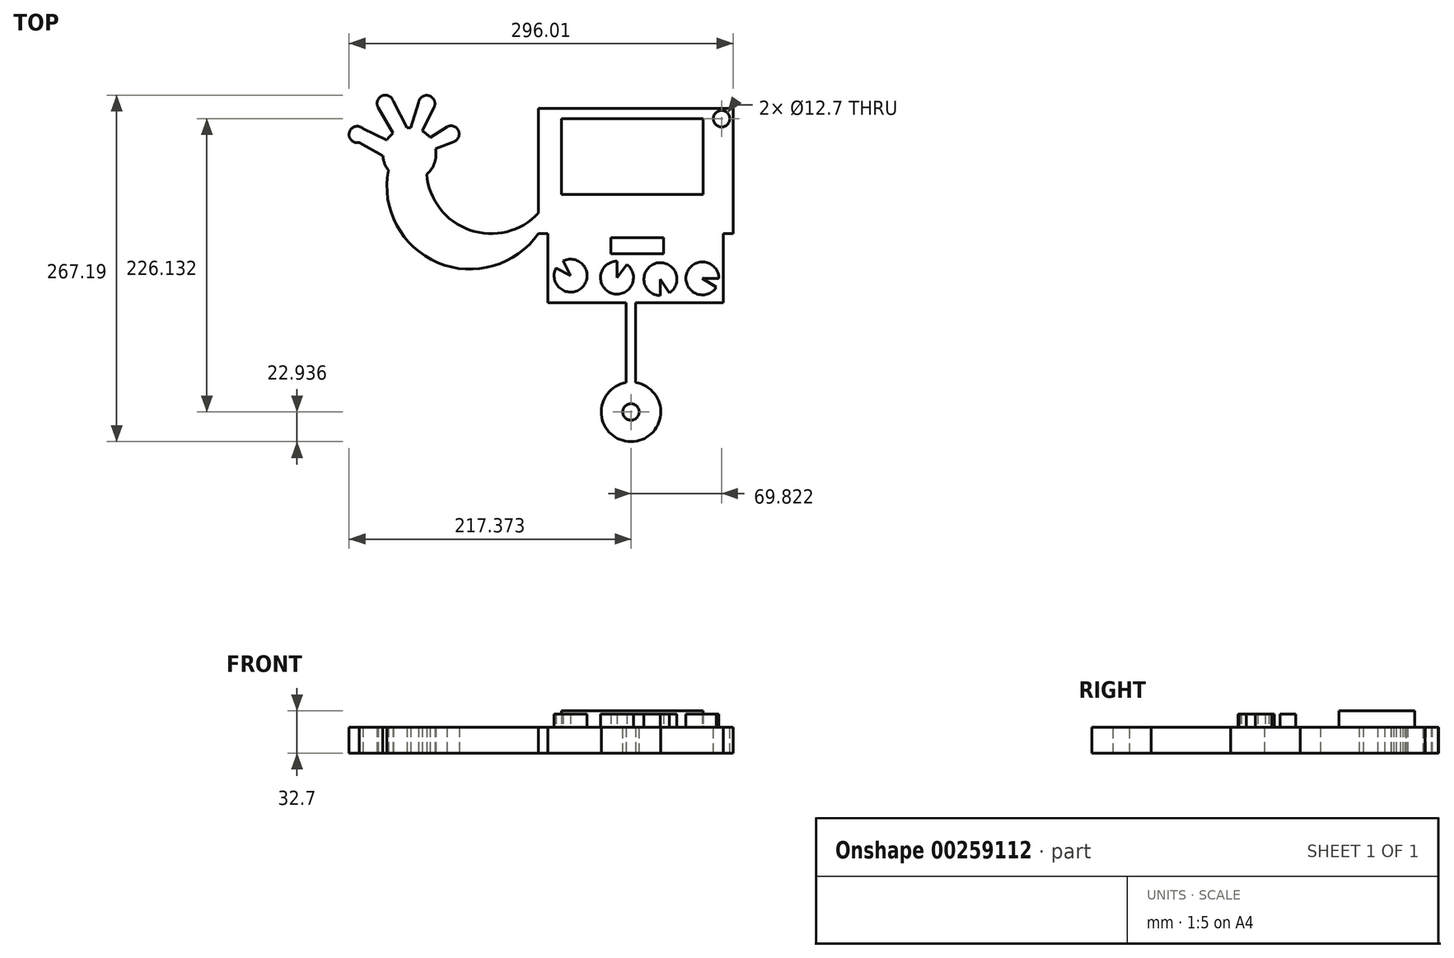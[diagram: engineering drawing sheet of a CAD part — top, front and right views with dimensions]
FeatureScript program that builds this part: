
annotation { "Feature Type Name" : "Feature", "Feature Type Description" : "" }
export const myFeature = defineFeature(function(context is Context, id is Id, definition is map)
    precondition{}
    {
        {
            var Q0;
            Q0=qCreatedBy(makeId("Top.planeOp"),FACE);
            var sketch = newSketch(context, id + "F0", { "sketchPlane" : qUnion([Q0])});
            skLineSegment(sketch, "E0.bottom", {"start": v(-67.58, -75) * mm, "end": v(67.58, -75) * mm});
            skLineSegment(sketch, "E0.top", {"start": v(-75, 75) * mm, "end": v(75, 75) * mm});
            skLineSegment(sketch, "E0.left", {"start": v(-75, -21.37) * mm, "end": v(-75, 75) * mm});
            skLineSegment(sketch, "E0.right", {"start": v(75, -21.37) * mm, "end": v(75, 75) * mm});
            skPoint(sketch, "E0.middle", {"position": v(0, 0) * mm});
            skLineSegment(sketch, "E1", {"start": v(-75, -21.37) * mm, "end": v(-67.58, -21.37) * mm});
            skLineSegment(sketch, "E2", {"start": v(-67.58, -21.37) * mm, "end": v(-67.58, -75) * mm});
            skLineSegment(sketch, "E3", {"start": v(67.58, -21.37) * mm, "end": v(75, -21.37) * mm});
            skLineSegment(sketch, "E4", {"start": v(67.58, -21.37) * mm, "end": v(67.58, -75) * mm});
            skLineSegment(sketch, "E5", {"start": v(-7.27, -75) * mm, "end": v(-7.27, -136.41) * mm});
            skCircle(sketch, "E6", {"center": v(-3.64, -159.05) * mm, "radius": 22.93 * mm});
            skCircle(sketch, "E7", {"center": v(-3.64, -159.05) * mm, "radius": 4.25 * mm});
            skLineSegment(sketch, "E8.trimOffspring", {"start": v(0, -136.41) * mm, "end": v(0, -75) * mm});
            skArc(sketch, "E9", {"start": v(-190.7, 27.24) * mm, "mid": v(-152.56, -43.97) * mm, "end": v(-75, -21.37) * mm});
            skLineSegment(sketch, "E10", {"start": v(0, -42.13) * mm, "end": v(0, -75) * mm, "construction": true});
            skArc(sketch, "E11.MirrorCS", {"start": v(190.7, 27.24) * mm, "mid": v(152.56, -43.97) * mm, "end": v(75, -21.37) * mm});
            skArc(sketch, "E12", {"start": v(-161.15, 24.18) * mm, "mid": v(-127.81, -18.85) * mm, "end": v(-75, -5.67) * mm});
            skArc(sketch, "E13.MirrorCS", {"start": v(161.15, 24.18) * mm, "mid": v(127.81, -18.85) * mm, "end": v(75, -5.67) * mm});
            skArc(sketch, "E14", {"start": v(-161.15, 24.18) * mm, "mid": v(-155.11, 33.1) * mm, "end": v(-154.43, 43.84) * mm});
            skArc(sketch, "E15.MirrorC", {"start": v(161.15, 24.18) * mm, "mid": v(155.11, 33.1) * mm, "end": v(154.43, 43.84) * mm});
            skArc(sketch, "E16", {"start": v(-210.14, 59.34) * mm, "mid": v(-220.78, 56.58) * mm, "end": v(-213.12, 48.7) * mm});
            skArc(sketch, "E17", {"start": v(-186.9, 80.39) * mm, "mid": v(-195.48, 84.73) * mm, "end": v(-198.53, 75.61) * mm});
            skArc(sketch, "E18", {"start": v(-155.48, 75.8) * mm, "mid": v(-159.23, 84.75) * mm, "end": v(-167.43, 79.57) * mm});
            skArc(sketch, "E19", {"start": v(-140.2, 49.3) * mm, "mid": v(-136.86, 58.2) * mm, "end": v(-146.08, 60.46) * mm});
            skLineSegment(sketch, "E20", {"start": v(-210.14, 59.34) * mm, "end": v(-191.76, 50.67) * mm});
            skLineSegment(sketch, "E21", {"start": v(-213.12, 48.7) * mm, "end": v(-194.9, 38.48) * mm});
            skArc(sketch, "E22.trimOffspring", {"start": v(-194.9, 38.48) * mm, "mid": v(-193.65, 32.54) * mm, "end": v(-190.7, 27.24) * mm});
            skLineSegment(sketch, "E23", {"start": v(-198.53, 75.61) * mm, "end": v(-187.14, 55.8) * mm});
            skLineSegment(sketch, "E24", {"start": v(-186.9, 80.39) * mm, "end": v(-176.4, 60.09) * mm});
            skArc(sketch, "E25.trimOffspring", {"start": v(-187.14, 55.8) * mm, "mid": v(-189.67, 53.43) * mm, "end": v(-191.76, 50.67) * mm});
            skLineSegment(sketch, "E26", {"start": v(-155.48, 75.8) * mm, "end": v(-164.74, 57.71) * mm});
            skLineSegment(sketch, "E27", {"start": v(-167.43, 79.57) * mm, "end": v(-173.43, 60.15) * mm});
            skArc(sketch, "E28.trimOffspring", {"start": v(-173.43, 60.15) * mm, "mid": v(-174.91, 60.18) * mm, "end": v(-176.4, 60.09) * mm});
            skLineSegment(sketch, "E29", {"start": v(-140.2, 49.3) * mm, "end": v(-154.43, 43.84) * mm});
            skLineSegment(sketch, "E30", {"start": v(-145.68, 60.72) * mm, "end": v(-158.55, 52.56) * mm});
            skArc(sketch, "E31.trimOffspring", {"start": v(-158.55, 52.56) * mm, "mid": v(-161.39, 55.45) * mm, "end": v(-164.74, 57.71) * mm});
            skArc(sketch, "E32.MirrorCS", {"start": v(187.14, 55.8) * mm, "mid": v(189.67, 53.43) * mm, "end": v(191.76, 50.67) * mm});
            skArc(sketch, "E33.MirrorCS", {"start": v(173.43, 60.15) * mm, "mid": v(174.91, 60.18) * mm, "end": v(176.4, 60.09) * mm});
            skArc(sketch, "E34.MirrorCS", {"start": v(158.55, 52.56) * mm, "mid": v(161.39, 55.45) * mm, "end": v(164.74, 57.71) * mm});
            skLineSegment(sketch, "E35.MirrorCS", {"start": v(198.53, 75.61) * mm, "end": v(187.14, 55.8) * mm});
            skArc(sketch, "E36.MirrorCS", {"start": v(210.14, 59.34) * mm, "mid": v(220.78, 56.58) * mm, "end": v(213.12, 48.7) * mm});
            skArc(sketch, "E37.MirrorCS", {"start": v(194.9, 38.48) * mm, "mid": v(193.65, 32.54) * mm, "end": v(190.7, 27.24) * mm});
            skArc(sketch, "E38.MirrorCS", {"start": v(140.2, 49.3) * mm, "mid": v(136.86, 58.2) * mm, "end": v(146.08, 60.46) * mm});
            skLineSegment(sketch, "E39.MirrorCS", {"start": v(140.2, 49.3) * mm, "end": v(154.43, 43.84) * mm});
            skLineSegment(sketch, "E40.MirrorCS", {"start": v(213.12, 48.7) * mm, "end": v(194.9, 38.48) * mm});
            skArc(sketch, "E41.MirrorCS", {"start": v(155.48, 75.8) * mm, "mid": v(159.23, 84.75) * mm, "end": v(167.43, 79.57) * mm});
            skLineSegment(sketch, "E42.MirrorCS", {"start": v(155.48, 75.8) * mm, "end": v(164.74, 57.71) * mm});
            skLineSegment(sketch, "E43.MirrorCS", {"start": v(145.68, 60.72) * mm, "end": v(158.55, 52.56) * mm});
            skArc(sketch, "E44.MirrorCS", {"start": v(186.9, 80.39) * mm, "mid": v(195.48, 84.73) * mm, "end": v(198.53, 75.61) * mm});
            skLineSegment(sketch, "E45.MirrorCS", {"start": v(186.9, 80.39) * mm, "end": v(176.4, 60.09) * mm});
            skLineSegment(sketch, "E46.MirrorCS", {"start": v(167.43, 79.57) * mm, "end": v(173.43, 60.15) * mm});
            skLineSegment(sketch, "E47.MirrorCS", {"start": v(210.14, 59.34) * mm, "end": v(191.76, 50.67) * mm});
            skPoint(sketch, "E48.orphan", {"position": v(-75, -75) * mm});
            skPoint(sketch, "E49.orphan", {"position": v(75, -75) * mm});
            skSolve(sketch);
        }
        {
            var Q0;
            {var subQ1=sQuery(id+"F0.wireOp",EDGE,"E0.top");Q0=makeQuery(id+"F0.imprint","IMPRINT",FACE,{"disambiguationData":[TD([[makeQuery(id+"F0.imprint","IMPRINT",EDGE,{"derivedFrom":subQ1}),-1.0]])]});}
            var Q1;
            {var subQ4=sQuery(id+"F0.wireOp",EDGE,"E9");Q1=makeQuery(id+"F0.imprint","IMPRINT",FACE,{"disambiguationData":[TD([[makeQuery(id+"F0.imprint","IMPRINT",EDGE,{"derivedFrom":subQ4}),1.0]])]});}
            var Q2;
            {var subQ6=sQuery(id+"F0.wireOp",EDGE,"E11.MirrorCS");Q2=makeQuery(id+"F0.imprint","IMPRINT",FACE,{"disambiguationData":[TD([[makeQuery(id+"F0.imprint","IMPRINT",EDGE,{"derivedFrom":subQ6}),-1.0]])]});}
            var Q3;
            {var subQ0=sQuery(id+"F0.wireOp",EDGE,"E5");Q3=makeQuery(id+"F0.imprint","IMPRINT",FACE,{"disambiguationData":[TD([[makeQuery(id+"F0.imprint","IMPRINT",EDGE,{"derivedFrom":subQ0}),1.0]])]});}
            var Q4;
            Q4=makeQuery(id+"F0.imprint","IMPRINT",FACE,{"disambiguationData":[TD([[makeQuery(id+"F0.imprint","IMPRINT",EDGE,{"derivedFrom":sQuery(id+"F0.wireOp",EDGE,"E7")}),-1.0]])]});
            var Q5;
            Q5=makeQuery(id+"F0.imprint","IMPRINT",FACE,{"disambiguationData":[TD([[makeQuery(id+"F0.imprint","IMPRINT",EDGE,{"derivedFrom":sQuery(id+"F0.wireOp",EDGE,"E7")}),1.0]])]});
            extrude(context, id + "F1", {"entities" : qUnion([Q0, Q1, Q2, Q3, Q4, Q5]), "depth" : 20 * mm});
        }
        {
            var Q0;
            Q0=makeQuery(id+"F1.opExtrude","CAP_FACE",FACE,{"disambiguationData":[OSD([sQuery(id+"F0.wireOp",EDGE,"E0.bottom"),sQuery(id+"F0.wireOp",EDGE,"E0.top"),sQuery(id+"F0.wireOp",EDGE,"E0.left"),sQuery(id+"F0.wireOp",EDGE,"E0.right"),sQuery(id+"F0.wireOp",EDGE,"E1"),sQuery(id+"F0.wireOp",EDGE,"E2"),sQuery(id+"F0.wireOp",EDGE,"E3"),sQuery(id+"F0.wireOp",EDGE,"E4"),sQuery(id+"F0.wireOp",EDGE,"E5"),sQuery(id+"F0.wireOp",EDGE,"E6"),sQuery(id+"F0.wireOp",EDGE,"E8.trimOffspring"),sQuery(id+"F0.wireOp",EDGE,"E9"),sQuery(id+"F0.wireOp",EDGE,"E11.MirrorCS"),sQuery(id+"F0.wireOp",EDGE,"E12"),sQuery(id+"F0.wireOp",EDGE,"E13.MirrorCS"),sQuery(id+"F0.wireOp",EDGE,"E14"),sQuery(id+"F0.wireOp",EDGE,"E16"),sQuery(id+"F0.wireOp",EDGE,"E17"),sQuery(id+"F0.wireOp",EDGE,"E18"),sQuery(id+"F0.wireOp",EDGE,"E19"),sQuery(id+"F0.wireOp",EDGE,"E20"),sQuery(id+"F0.wireOp",EDGE,"E21"),sQuery(id+"F0.wireOp",EDGE,"E22.trimOffspring"),sQuery(id+"F0.wireOp",EDGE,"E23"),sQuery(id+"F0.wireOp",EDGE,"E24"),sQuery(id+"F0.wireOp",EDGE,"E25.trimOffspring"),sQuery(id+"F0.wireOp",EDGE,"E26"),sQuery(id+"F0.wireOp",EDGE,"E27"),sQuery(id+"F0.wireOp",EDGE,"E28.trimOffspring"),sQuery(id+"F0.wireOp",EDGE,"E29"),sQuery(id+"F0.wireOp",EDGE,"E30"),sQuery(id+"F0.wireOp",EDGE,"E31.trimOffspring"),sQuery(id+"F0.wireOp",EDGE,"E35.MirrorCS"),sQuery(id+"F0.wireOp",EDGE,"E36.MirrorCS"),sQuery(id+"F0.wireOp",EDGE,"E15.MirrorC"),sQuery(id+"F0.wireOp",EDGE,"E38.MirrorCS"),sQuery(id+"F0.wireOp",EDGE,"E39.MirrorCS"),sQuery(id+"F0.wireOp",EDGE,"E40.MirrorCS"),sQuery(id+"F0.wireOp",EDGE,"E41.MirrorCS"),sQuery(id+"F0.wireOp",EDGE,"E42.MirrorCS"),sQuery(id+"F0.wireOp",EDGE,"E43.MirrorCS"),sQuery(id+"F0.wireOp",EDGE,"E44.MirrorCS"),sQuery(id+"F0.wireOp",EDGE,"E45.MirrorCS"),sQuery(id+"F0.wireOp",EDGE,"E46.MirrorCS"),sQuery(id+"F0.wireOp",EDGE,"E47.MirrorCS"),sQuery(id+"F0.wireOp",EDGE,"E34.MirrorCS"),sQuery(id+"F0.wireOp",EDGE,"E33.MirrorCS"),sQuery(id+"F0.wireOp",EDGE,"E32.MirrorCS"),sQuery(id+"F0.wireOp",EDGE,"E37.MirrorCS")])],"isStart":false});
            var sketch = newSketch(context, id + "F2", { "sketchPlane" : qUnion([Q0])});
            skLineSegment(sketch, "E50.bottom", {"start": v(-19.06, -24.75) * mm, "end": v(21.38, -24.75) * mm});
            skLineSegment(sketch, "E50.top", {"start": v(-19.06, -37.01) * mm, "end": v(21.38, -37.01) * mm});
            skLineSegment(sketch, "E50.left", {"start": v(-19.06, -24.75) * mm, "end": v(-19.06, -37.01) * mm});
            skLineSegment(sketch, "E50.right", {"start": v(21.38, -24.75) * mm, "end": v(21.38, -37.01) * mm});
            skLineSegment(sketch, "E51", {"start": v(-8.67, -24.75) * mm, "end": v(-8.67, -37.01) * mm});
            skLineSegment(sketch, "E52", {"start": v(1.16, -24.75) * mm, "end": v(1.16, -37.01) * mm});
            skLineSegment(sketch, "E53", {"start": v(10.4, -24.75) * mm, "end": v(10.4, -37.01) * mm});
            skArc(sketch, "E54", {"start": v(-61.54, -48.19) * mm, "mid": v(-41.29, -62.98) * mm, "end": v(-55.89, -42.58) * mm});
            skArc(sketch, "E55", {"start": v(-14.44, -42.8) * mm, "mid": v(-18.53, -67.53) * mm, "end": v(-6.7, -45.43) * mm});
            skArc(sketch, "E56", {"start": v(26.07, -67.25) * mm, "mid": v(15.4, -44.5) * mm, "end": v(19.07, -69.36) * mm});
            skArc(sketch, "E57", {"start": v(64.12, -56.08) * mm, "mid": v(39.22, -52.55) * mm, "end": v(62.16, -62.86) * mm});
            skPoint(sketch, "E58.startSnap0", {"position": v(-67.58, -48.19) * mm});
            skLineSegment(sketch, "E59", {"start": v(-55.89, -42.58) * mm, "end": v(-50.23, -53.95) * mm});
            skPoint(sketch, "E59.startSnap0", {"position": v(-55.89, -51.07) * mm});
            skLineSegment(sketch, "E60", {"start": v(-14.44, -55.5) * mm, "end": v(-14.44, -42.8) * mm});
            skLineSegment(sketch, "E61", {"start": v(-14.44, -55.5) * mm, "end": v(-6.7, -45.43) * mm});
            skLineSegment(sketch, "E62", {"start": v(19.07, -56.66) * mm, "end": v(19.07, -69.36) * mm});
            skLineSegment(sketch, "E63", {"start": v(19.07, -56.66) * mm, "end": v(26.07, -67.25) * mm});
            skLineSegment(sketch, "E64", {"start": v(51.42, -56.08) * mm, "end": v(64.12, -56.08) * mm});
            skLineSegment(sketch, "E65", {"start": v(64.12, -56.08) * mm, "end": v(51.42, -56.08) * mm});
            skLineSegment(sketch, "E66", {"start": v(51.42, -56.08) * mm, "end": v(62.16, -62.86) * mm});
            skPoint(sketch, "E67.orphan", {"position": v(-61.54, -48.19) * mm});
            skLineSegment(sketch, "E68", {"start": v(-61.54, -48.19) * mm, "end": v(-50.23, -53.95) * mm});
            skSolve(sketch);
        }
        {
            var Q0;
            Q0 = qSketchRegion(id + "F2", true);
            extrude(context, id + "F3", {"entities" : qUnion([Q0]), "operationType" : NewBodyOperationType.ADD, "depth" : 10.16 * mm});
        }
        {
            var Q0;
            Q0=makeQuery(id+"F1.opExtrude","CAP_FACE",FACE,{"disambiguationData":[OSD([sQuery(id+"F0.wireOp",EDGE,"E0.bottom"),sQuery(id+"F0.wireOp",EDGE,"E0.top"),sQuery(id+"F0.wireOp",EDGE,"E0.left"),sQuery(id+"F0.wireOp",EDGE,"E0.right"),sQuery(id+"F0.wireOp",EDGE,"E1"),sQuery(id+"F0.wireOp",EDGE,"E2"),sQuery(id+"F0.wireOp",EDGE,"E3"),sQuery(id+"F0.wireOp",EDGE,"E4"),sQuery(id+"F0.wireOp",EDGE,"E5"),sQuery(id+"F0.wireOp",EDGE,"E6"),sQuery(id+"F0.wireOp",EDGE,"E8.trimOffspring"),sQuery(id+"F0.wireOp",EDGE,"E9"),sQuery(id+"F0.wireOp",EDGE,"E11.MirrorCS"),sQuery(id+"F0.wireOp",EDGE,"E12"),sQuery(id+"F0.wireOp",EDGE,"E13.MirrorCS"),sQuery(id+"F0.wireOp",EDGE,"E14"),sQuery(id+"F0.wireOp",EDGE,"E16"),sQuery(id+"F0.wireOp",EDGE,"E17"),sQuery(id+"F0.wireOp",EDGE,"E18"),sQuery(id+"F0.wireOp",EDGE,"E19"),sQuery(id+"F0.wireOp",EDGE,"E20"),sQuery(id+"F0.wireOp",EDGE,"E21"),sQuery(id+"F0.wireOp",EDGE,"E22.trimOffspring"),sQuery(id+"F0.wireOp",EDGE,"E23"),sQuery(id+"F0.wireOp",EDGE,"E24"),sQuery(id+"F0.wireOp",EDGE,"E25.trimOffspring"),sQuery(id+"F0.wireOp",EDGE,"E26"),sQuery(id+"F0.wireOp",EDGE,"E27"),sQuery(id+"F0.wireOp",EDGE,"E28.trimOffspring"),sQuery(id+"F0.wireOp",EDGE,"E29"),sQuery(id+"F0.wireOp",EDGE,"E30"),sQuery(id+"F0.wireOp",EDGE,"E31.trimOffspring"),sQuery(id+"F0.wireOp",EDGE,"E35.MirrorCS"),sQuery(id+"F0.wireOp",EDGE,"E36.MirrorCS"),sQuery(id+"F0.wireOp",EDGE,"E15.MirrorC"),sQuery(id+"F0.wireOp",EDGE,"E38.MirrorCS"),sQuery(id+"F0.wireOp",EDGE,"E39.MirrorCS"),sQuery(id+"F0.wireOp",EDGE,"E40.MirrorCS"),sQuery(id+"F0.wireOp",EDGE,"E41.MirrorCS"),sQuery(id+"F0.wireOp",EDGE,"E42.MirrorCS"),sQuery(id+"F0.wireOp",EDGE,"E43.MirrorCS"),sQuery(id+"F0.wireOp",EDGE,"E44.MirrorCS"),sQuery(id+"F0.wireOp",EDGE,"E45.MirrorCS"),sQuery(id+"F0.wireOp",EDGE,"E46.MirrorCS"),sQuery(id+"F0.wireOp",EDGE,"E47.MirrorCS"),sQuery(id+"F0.wireOp",EDGE,"E34.MirrorCS"),sQuery(id+"F0.wireOp",EDGE,"E33.MirrorCS"),sQuery(id+"F0.wireOp",EDGE,"E32.MirrorCS"),sQuery(id+"F0.wireOp",EDGE,"E37.MirrorCS")])],"isStart":false});
            var sketch = newSketch(context, id + "F4", { "sketchPlane" : qUnion([Q0])});
            skLineSegment(sketch, "E69.bottom", {"start": v(-57.22, 67.08) * mm, "end": v(52, 67.08) * mm});
            skLineSegment(sketch, "E69.top", {"start": v(-57.22, 8.66) * mm, "end": v(52, 8.66) * mm});
            skLineSegment(sketch, "E69.left", {"start": v(-57.22, 67.08) * mm, "end": v(-57.22, 8.66) * mm});
            skLineSegment(sketch, "E69.right", {"start": v(52, 67.08) * mm, "end": v(52, 8.66) * mm});
            skSolve(sketch);
        }
        {
            var Q0;
            Q0=makeQuery(id+"F1.opExtrude","CAP_FACE",FACE,{"disambiguationData":[OSD([sQuery(id+"F0.wireOp",EDGE,"E0.bottom"),sQuery(id+"F0.wireOp",EDGE,"E0.top"),sQuery(id+"F0.wireOp",EDGE,"E0.left"),sQuery(id+"F0.wireOp",EDGE,"E0.right"),sQuery(id+"F0.wireOp",EDGE,"E1"),sQuery(id+"F0.wireOp",EDGE,"E2"),sQuery(id+"F0.wireOp",EDGE,"E3"),sQuery(id+"F0.wireOp",EDGE,"E4"),sQuery(id+"F0.wireOp",EDGE,"E5"),sQuery(id+"F0.wireOp",EDGE,"E6"),sQuery(id+"F0.wireOp",EDGE,"E8.trimOffspring"),sQuery(id+"F0.wireOp",EDGE,"E9"),sQuery(id+"F0.wireOp",EDGE,"E11.MirrorCS"),sQuery(id+"F0.wireOp",EDGE,"E12"),sQuery(id+"F0.wireOp",EDGE,"E13.MirrorCS"),sQuery(id+"F0.wireOp",EDGE,"E14"),sQuery(id+"F0.wireOp",EDGE,"E16"),sQuery(id+"F0.wireOp",EDGE,"E17"),sQuery(id+"F0.wireOp",EDGE,"E18"),sQuery(id+"F0.wireOp",EDGE,"E19"),sQuery(id+"F0.wireOp",EDGE,"E20"),sQuery(id+"F0.wireOp",EDGE,"E21"),sQuery(id+"F0.wireOp",EDGE,"E22.trimOffspring"),sQuery(id+"F0.wireOp",EDGE,"E23"),sQuery(id+"F0.wireOp",EDGE,"E24"),sQuery(id+"F0.wireOp",EDGE,"E25.trimOffspring"),sQuery(id+"F0.wireOp",EDGE,"E26"),sQuery(id+"F0.wireOp",EDGE,"E27"),sQuery(id+"F0.wireOp",EDGE,"E28.trimOffspring"),sQuery(id+"F0.wireOp",EDGE,"E29"),sQuery(id+"F0.wireOp",EDGE,"E30"),sQuery(id+"F0.wireOp",EDGE,"E31.trimOffspring"),sQuery(id+"F0.wireOp",EDGE,"E35.MirrorCS"),sQuery(id+"F0.wireOp",EDGE,"E36.MirrorCS"),sQuery(id+"F0.wireOp",EDGE,"E15.MirrorC"),sQuery(id+"F0.wireOp",EDGE,"E38.MirrorCS"),sQuery(id+"F0.wireOp",EDGE,"E39.MirrorCS"),sQuery(id+"F0.wireOp",EDGE,"E40.MirrorCS"),sQuery(id+"F0.wireOp",EDGE,"E41.MirrorCS"),sQuery(id+"F0.wireOp",EDGE,"E42.MirrorCS"),sQuery(id+"F0.wireOp",EDGE,"E43.MirrorCS"),sQuery(id+"F0.wireOp",EDGE,"E44.MirrorCS"),sQuery(id+"F0.wireOp",EDGE,"E45.MirrorCS"),sQuery(id+"F0.wireOp",EDGE,"E46.MirrorCS"),sQuery(id+"F0.wireOp",EDGE,"E47.MirrorCS"),sQuery(id+"F0.wireOp",EDGE,"E34.MirrorCS"),sQuery(id+"F0.wireOp",EDGE,"E33.MirrorCS"),sQuery(id+"F0.wireOp",EDGE,"E32.MirrorCS"),sQuery(id+"F0.wireOp",EDGE,"E37.MirrorCS")])],"isStart":false});
            var sketch = newSketch(context, id + "F5", { "sketchPlane" : qUnion([Q0])});
            skCircle(sketch, "E70", {"center": v(-3.64, -159.05) * mm, "radius": 6.35 * mm});
            skSolve(sketch);
        }
        {
            var Q0;
            Q0=makeQuery(id+"F5.imprint","IMPRINT",FACE,{"disambiguationData":[TD([[makeQuery(id+"F5.imprint","IMPRINT",EDGE,{"derivedFrom":sQuery(id+"F5.wireOp",EDGE,"E70")}),1.0]])]});
            extrude(context, id + "F6", {"entities" : qUnion([Q0]), "operationType" : NewBodyOperationType.REMOVE, "oppositeDirection" : true, "depth" : 25.4 * mm});
        }
        {
            var Q0;
            Q0=makeQuery(id+"F1.opExtrude","CAP_FACE",FACE,{"disambiguationData":[OSD([sQuery(id+"F0.wireOp",EDGE,"E0.bottom"),sQuery(id+"F0.wireOp",EDGE,"E0.top"),sQuery(id+"F0.wireOp",EDGE,"E0.left"),sQuery(id+"F0.wireOp",EDGE,"E0.right"),sQuery(id+"F0.wireOp",EDGE,"E1"),sQuery(id+"F0.wireOp",EDGE,"E2"),sQuery(id+"F0.wireOp",EDGE,"E3"),sQuery(id+"F0.wireOp",EDGE,"E4"),sQuery(id+"F0.wireOp",EDGE,"E5"),sQuery(id+"F0.wireOp",EDGE,"E6"),sQuery(id+"F0.wireOp",EDGE,"E8.trimOffspring"),sQuery(id+"F0.wireOp",EDGE,"E9"),sQuery(id+"F0.wireOp",EDGE,"E11.MirrorCS"),sQuery(id+"F0.wireOp",EDGE,"E12"),sQuery(id+"F0.wireOp",EDGE,"E13.MirrorCS"),sQuery(id+"F0.wireOp",EDGE,"E14"),sQuery(id+"F0.wireOp",EDGE,"E16"),sQuery(id+"F0.wireOp",EDGE,"E17"),sQuery(id+"F0.wireOp",EDGE,"E18"),sQuery(id+"F0.wireOp",EDGE,"E19"),sQuery(id+"F0.wireOp",EDGE,"E20"),sQuery(id+"F0.wireOp",EDGE,"E21"),sQuery(id+"F0.wireOp",EDGE,"E22.trimOffspring"),sQuery(id+"F0.wireOp",EDGE,"E23"),sQuery(id+"F0.wireOp",EDGE,"E24"),sQuery(id+"F0.wireOp",EDGE,"E25.trimOffspring"),sQuery(id+"F0.wireOp",EDGE,"E26"),sQuery(id+"F0.wireOp",EDGE,"E27"),sQuery(id+"F0.wireOp",EDGE,"E28.trimOffspring"),sQuery(id+"F0.wireOp",EDGE,"E29"),sQuery(id+"F0.wireOp",EDGE,"E30"),sQuery(id+"F0.wireOp",EDGE,"E31.trimOffspring"),sQuery(id+"F0.wireOp",EDGE,"E35.MirrorCS"),sQuery(id+"F0.wireOp",EDGE,"E36.MirrorCS"),sQuery(id+"F0.wireOp",EDGE,"E15.MirrorC"),sQuery(id+"F0.wireOp",EDGE,"E38.MirrorCS"),sQuery(id+"F0.wireOp",EDGE,"E39.MirrorCS"),sQuery(id+"F0.wireOp",EDGE,"E40.MirrorCS"),sQuery(id+"F0.wireOp",EDGE,"E41.MirrorCS"),sQuery(id+"F0.wireOp",EDGE,"E42.MirrorCS"),sQuery(id+"F0.wireOp",EDGE,"E43.MirrorCS"),sQuery(id+"F0.wireOp",EDGE,"E44.MirrorCS"),sQuery(id+"F0.wireOp",EDGE,"E45.MirrorCS"),sQuery(id+"F0.wireOp",EDGE,"E46.MirrorCS"),sQuery(id+"F0.wireOp",EDGE,"E47.MirrorCS"),sQuery(id+"F0.wireOp",EDGE,"E34.MirrorCS"),sQuery(id+"F0.wireOp",EDGE,"E33.MirrorCS"),sQuery(id+"F0.wireOp",EDGE,"E32.MirrorCS"),sQuery(id+"F0.wireOp",EDGE,"E37.MirrorCS")])],"isStart":false});
            var sketch = newSketch(context, id + "F7", { "sketchPlane" : qUnion([Q0])});
            skCircle(sketch, "E71", {"center": v(66.19, 67.08) * mm, "radius": 6.35 * mm});
            skSolve(sketch);
        }
        {
            var Q0;
            Q0=makeQuery(id+"F7.imprint","IMPRINT",FACE,{"disambiguationData":[TD([[makeQuery(id+"F7.imprint","IMPRINT",EDGE,{"derivedFrom":sQuery(id+"F7.wireOp",EDGE,"E71")}),1.0]])]});
            extrude(context, id + "F8", {"entities" : qUnion([Q0]), "operationType" : NewBodyOperationType.REMOVE, "oppositeDirection" : true, "depth" : 25.4 * mm});
        }
        {
            var Q0;
            {var subQ0=sQuery(id+"F4.wireOp",EDGE,"E69.left");var subQ1=sQuery(id+"F4.wireOp",EDGE,"E69.bottom");var subQ2=makeQuery(id+"F4.imprint","INTERSECT",VERTEX,{"derivedFrom":[subQ1,subQ0]});Q0=makeQuery(id+"F4.imprint","IMPRINT",FACE,{"disambiguationData":[TD([[makeQuery(id+"F4.imprint","IMPRINT",EDGE,{"disambiguationData":[TD([[subQ2,-1.0]])],"derivedFrom":subQ1}),-1.0]])]});}
            var Q1;
            {var subQ0=sQuery(id+"F4.wireOp",EDGE,"6969bc10-0764-4b5e-9f94-18c3d4fac763");var subQ1=sQuery(id+"F4.wireOp",EDGE,"E69.bottom");var subQ2=makeQuery(id+"F4.imprint","INTERSECT",VERTEX,{"derivedFrom":[subQ1,subQ0]});Q1=makeQuery(id+"F4.imprint","IMPRINT",FACE,{"disambiguationData":[TD([[makeQuery(id+"F4.imprint","IMPRINT",EDGE,{"disambiguationData":[TD([[subQ2,-1.0]])],"derivedFrom":subQ1}),-1.0]])]});}
            var Q2;
            {var subQ0=sQuery(id+"F4.wireOp",EDGE,"04714c49-f67c-4b11-ac7b-a62ad5dfcefc");var subQ1=sQuery(id+"F4.wireOp",EDGE,"E69.bottom");var subQ2=makeQuery(id+"F4.imprint","INTERSECT",VERTEX,{"derivedFrom":[subQ1,subQ0]});Q2=makeQuery(id+"F4.imprint","IMPRINT",FACE,{"disambiguationData":[TD([[makeQuery(id+"F4.imprint","IMPRINT",EDGE,{"disambiguationData":[TD([[subQ2,-1.0]])],"derivedFrom":subQ1}),-1.0]])]});}
            var Q3;
            {var subQ0=sQuery(id+"F4.wireOp",EDGE,"31bb1669-3a15-43ee-9b4d-b7e116c8bd2d");var subQ1=sQuery(id+"F4.wireOp",EDGE,"E69.bottom");var subQ2=makeQuery(id+"F4.imprint","INTERSECT",VERTEX,{"derivedFrom":[subQ1,subQ0]});Q3=makeQuery(id+"F4.imprint","IMPRINT",FACE,{"disambiguationData":[TD([[makeQuery(id+"F4.imprint","IMPRINT",EDGE,{"disambiguationData":[TD([[subQ2,-1.0]])],"derivedFrom":subQ1}),-1.0]])]});}
            var Q4;
            {var subQ0=sQuery(id+"F4.wireOp",EDGE,"f07b2809-b0b2-432a-b4bd-e478a1343b42");var subQ1=sQuery(id+"F4.wireOp",EDGE,"E69.bottom");var subQ2=makeQuery(id+"F4.imprint","INTERSECT",VERTEX,{"derivedFrom":[subQ1,subQ0]});Q4=makeQuery(id+"F4.imprint","IMPRINT",FACE,{"disambiguationData":[TD([[makeQuery(id+"F4.imprint","IMPRINT",EDGE,{"disambiguationData":[TD([[subQ2,-1.0]])],"derivedFrom":subQ1}),-1.0]])]});}
            var Q5;
            {var subQ0=sQuery(id+"F4.wireOp",EDGE,"E69.right");var subQ1=sQuery(id+"F4.wireOp",EDGE,"E69.bottom");var subQ2=makeQuery(id+"F4.imprint","INTERSECT",VERTEX,{"derivedFrom":[subQ1,subQ0]});Q5=makeQuery(id+"F4.imprint","IMPRINT",FACE,{"disambiguationData":[TD([[makeQuery(id+"F4.imprint","IMPRINT",EDGE,{"disambiguationData":[TD([[subQ2,1.0]])],"derivedFrom":subQ1}),-1.0]])]});}
            var Q6;
            {var subQ0=sQuery(id+"F4.wireOp",EDGE,"a4a6697a-bb5a-402e-a274-67412d378b00");var subQ1=sQuery(id+"F4.wireOp",EDGE,"E69.right");var subQ2=makeQuery(id+"F4.imprint","INTERSECT",VERTEX,{"derivedFrom":[subQ1,subQ0]});Q6=makeQuery(id+"F4.imprint","IMPRINT",FACE,{"disambiguationData":[TD([[makeQuery(id+"F4.imprint","IMPRINT",EDGE,{"disambiguationData":[TD([[subQ2,-1.0]])],"derivedFrom":subQ1}),-1.0]])]});}
            var Q7;
            {var subQ0=sQuery(id+"F4.wireOp",EDGE,"bd874a56-4970-42b9-9756-858d7ebeb413");var subQ1=sQuery(id+"F4.wireOp",EDGE,"E69.right");var subQ2=makeQuery(id+"F4.imprint","INTERSECT",VERTEX,{"derivedFrom":[subQ1,subQ0]});Q7=makeQuery(id+"F4.imprint","IMPRINT",FACE,{"disambiguationData":[TD([[makeQuery(id+"F4.imprint","IMPRINT",EDGE,{"disambiguationData":[TD([[subQ2,-1.0]])],"derivedFrom":subQ1}),-1.0]])]});}
            var Q8;
            {var subQ0=sQuery(id+"F4.wireOp",EDGE,"E69.right");var subQ1=sQuery(id+"F4.wireOp",EDGE,"E69.top");var subQ2=makeQuery(id+"F4.imprint","INTERSECT",VERTEX,{"derivedFrom":[subQ1,subQ0]});Q8=makeQuery(id+"F4.imprint","IMPRINT",FACE,{"disambiguationData":[TD([[makeQuery(id+"F4.imprint","IMPRINT",EDGE,{"disambiguationData":[TD([[subQ2,1.0]])],"derivedFrom":subQ1}),1.0]])]});}
            var Q9;
            {var subQ0=sQuery(id+"F4.wireOp",EDGE,"f07b2809-b0b2-432a-b4bd-e478a1343b42");var subQ1=sQuery(id+"F4.wireOp",EDGE,"E69.top");var subQ2=makeQuery(id+"F4.imprint","INTERSECT",VERTEX,{"derivedFrom":[subQ1,subQ0]});Q9=makeQuery(id+"F4.imprint","IMPRINT",FACE,{"disambiguationData":[TD([[makeQuery(id+"F4.imprint","IMPRINT",EDGE,{"disambiguationData":[TD([[subQ2,-1.0]])],"derivedFrom":subQ1}),1.0]])]});}
            var Q10;
            {var subQ0=sQuery(id+"F4.wireOp",EDGE,"bd874a56-4970-42b9-9756-858d7ebeb413");var subQ1=sQuery(id+"F4.wireOp",EDGE,"f07b2809-b0b2-432a-b4bd-e478a1343b42");var subQ2=makeQuery(id+"F4.imprint","INTERSECT",VERTEX,{"derivedFrom":[subQ1,subQ0]});Q10=makeQuery(id+"F4.imprint","IMPRINT",FACE,{"disambiguationData":[TD([[makeQuery(id+"F4.imprint","IMPRINT",EDGE,{"disambiguationData":[TD([[subQ2,-1.0]])],"derivedFrom":subQ1}),1.0]])]});}
            var Q11;
            {var subQ0=sQuery(id+"F4.wireOp",EDGE,"a4a6697a-bb5a-402e-a274-67412d378b00");var subQ1=sQuery(id+"F4.wireOp",EDGE,"f07b2809-b0b2-432a-b4bd-e478a1343b42");var subQ2=makeQuery(id+"F4.imprint","INTERSECT",VERTEX,{"derivedFrom":[subQ1,subQ0]});Q11=makeQuery(id+"F4.imprint","IMPRINT",FACE,{"disambiguationData":[TD([[makeQuery(id+"F4.imprint","IMPRINT",EDGE,{"disambiguationData":[TD([[subQ2,-1.0]])],"derivedFrom":subQ1}),1.0]])]});}
            var Q12;
            {var subQ0=sQuery(id+"F4.wireOp",EDGE,"bd874a56-4970-42b9-9756-858d7ebeb413");var subQ1=sQuery(id+"F4.wireOp",EDGE,"04714c49-f67c-4b11-ac7b-a62ad5dfcefc");var subQ2=makeQuery(id+"F4.imprint","INTERSECT",VERTEX,{"derivedFrom":[subQ1,subQ0]});Q12=makeQuery(id+"F4.imprint","IMPRINT",FACE,{"disambiguationData":[TD([[makeQuery(id+"F4.imprint","IMPRINT",EDGE,{"disambiguationData":[TD([[subQ2,-1.0]])],"derivedFrom":subQ1}),-1.0]])]});}
            var Q13;
            {var subQ0=sQuery(id+"F4.wireOp",EDGE,"1a1e249b-4780-4803-a19b-28437fd310a8");var subQ1=sQuery(id+"F4.wireOp",EDGE,"04714c49-f67c-4b11-ac7b-a62ad5dfcefc");var subQ2=makeQuery(id+"F4.imprint","INTERSECT",VERTEX,{"derivedFrom":[subQ1,subQ0]});Q13=makeQuery(id+"F4.imprint","IMPRINT",FACE,{"disambiguationData":[TD([[makeQuery(id+"F4.imprint","IMPRINT",EDGE,{"disambiguationData":[TD([[subQ2,-1.0]])],"derivedFrom":subQ1}),-1.0]])]});}
            var Q14;
            {var subQ0=sQuery(id+"F4.wireOp",EDGE,"04714c49-f67c-4b11-ac7b-a62ad5dfcefc");var subQ1=sQuery(id+"F4.wireOp",EDGE,"E69.top");var subQ2=makeQuery(id+"F4.imprint","INTERSECT",VERTEX,{"derivedFrom":[subQ1,subQ0]});Q14=makeQuery(id+"F4.imprint","IMPRINT",FACE,{"disambiguationData":[TD([[makeQuery(id+"F4.imprint","IMPRINT",EDGE,{"disambiguationData":[TD([[subQ2,-1.0]])],"derivedFrom":subQ1}),1.0]])]});}
            var Q15;
            {var subQ0=sQuery(id+"F4.wireOp",EDGE,"31bb1669-3a15-43ee-9b4d-b7e116c8bd2d");var subQ1=sQuery(id+"F4.wireOp",EDGE,"E69.top");var subQ2=makeQuery(id+"F4.imprint","INTERSECT",VERTEX,{"derivedFrom":[subQ1,subQ0]});Q15=makeQuery(id+"F4.imprint","IMPRINT",FACE,{"disambiguationData":[TD([[makeQuery(id+"F4.imprint","IMPRINT",EDGE,{"disambiguationData":[TD([[subQ2,-1.0]])],"derivedFrom":subQ1}),1.0]])]});}
            var Q16;
            {var subQ0=sQuery(id+"F4.wireOp",EDGE,"1a1e249b-4780-4803-a19b-28437fd310a8");var subQ1=sQuery(id+"F4.wireOp",EDGE,"31bb1669-3a15-43ee-9b4d-b7e116c8bd2d");var subQ2=makeQuery(id+"F4.imprint","INTERSECT",VERTEX,{"derivedFrom":[subQ1,subQ0]});Q16=makeQuery(id+"F4.imprint","IMPRINT",FACE,{"disambiguationData":[TD([[makeQuery(id+"F4.imprint","IMPRINT",EDGE,{"disambiguationData":[TD([[subQ2,-1.0]])],"derivedFrom":subQ1}),-1.0]])]});}
            var Q17;
            {var subQ0=sQuery(id+"F4.wireOp",EDGE,"bd874a56-4970-42b9-9756-858d7ebeb413");var subQ1=sQuery(id+"F4.wireOp",EDGE,"31bb1669-3a15-43ee-9b4d-b7e116c8bd2d");var subQ2=makeQuery(id+"F4.imprint","INTERSECT",VERTEX,{"derivedFrom":[subQ1,subQ0]});Q17=makeQuery(id+"F4.imprint","IMPRINT",FACE,{"disambiguationData":[TD([[makeQuery(id+"F4.imprint","IMPRINT",EDGE,{"disambiguationData":[TD([[subQ2,-1.0]])],"derivedFrom":subQ1}),-1.0]])]});}
            var Q18;
            {var subQ0=sQuery(id+"F4.wireOp",EDGE,"a4a6697a-bb5a-402e-a274-67412d378b00");var subQ1=sQuery(id+"F4.wireOp",EDGE,"6969bc10-0764-4b5e-9f94-18c3d4fac763");var subQ2=makeQuery(id+"F4.imprint","INTERSECT",VERTEX,{"derivedFrom":[subQ1,subQ0]});Q18=makeQuery(id+"F4.imprint","IMPRINT",FACE,{"disambiguationData":[TD([[makeQuery(id+"F4.imprint","IMPRINT",EDGE,{"disambiguationData":[TD([[subQ2,-1.0]])],"derivedFrom":subQ1}),1.0]])]});}
            var Q19;
            {var subQ0=sQuery(id+"F4.wireOp",EDGE,"bd874a56-4970-42b9-9756-858d7ebeb413");var subQ1=sQuery(id+"F4.wireOp",EDGE,"6969bc10-0764-4b5e-9f94-18c3d4fac763");var subQ2=makeQuery(id+"F4.imprint","INTERSECT",VERTEX,{"derivedFrom":[subQ1,subQ0]});Q19=makeQuery(id+"F4.imprint","IMPRINT",FACE,{"disambiguationData":[TD([[makeQuery(id+"F4.imprint","IMPRINT",EDGE,{"disambiguationData":[TD([[subQ2,-1.0]])],"derivedFrom":subQ1}),1.0]])]});}
            var Q20;
            {var subQ0=sQuery(id+"F4.wireOp",EDGE,"6969bc10-0764-4b5e-9f94-18c3d4fac763");var subQ1=sQuery(id+"F4.wireOp",EDGE,"E69.top");var subQ2=makeQuery(id+"F4.imprint","INTERSECT",VERTEX,{"derivedFrom":[subQ1,subQ0]});Q20=makeQuery(id+"F4.imprint","IMPRINT",FACE,{"disambiguationData":[TD([[makeQuery(id+"F4.imprint","IMPRINT",EDGE,{"disambiguationData":[TD([[subQ2,-1.0]])],"derivedFrom":subQ1}),1.0]])]});}
            var Q21;
            {var subQ0=sQuery(id+"F4.wireOp",EDGE,"E69.left");var subQ1=sQuery(id+"F4.wireOp",EDGE,"E69.top");var subQ2=makeQuery(id+"F4.imprint","INTERSECT",VERTEX,{"derivedFrom":[subQ1,subQ0]});Q21=makeQuery(id+"F4.imprint","IMPRINT",FACE,{"disambiguationData":[TD([[makeQuery(id+"F4.imprint","IMPRINT",EDGE,{"disambiguationData":[TD([[subQ2,-1.0]])],"derivedFrom":subQ1}),1.0]])]});}
            var Q22;
            {var subQ0=sQuery(id+"F4.wireOp",EDGE,"bd874a56-4970-42b9-9756-858d7ebeb413");var subQ1=sQuery(id+"F4.wireOp",EDGE,"E69.left");var subQ2=makeQuery(id+"F4.imprint","INTERSECT",VERTEX,{"derivedFrom":[subQ1,subQ0]});Q22=makeQuery(id+"F4.imprint","IMPRINT",FACE,{"disambiguationData":[TD([[makeQuery(id+"F4.imprint","IMPRINT",EDGE,{"disambiguationData":[TD([[subQ2,-1.0]])],"derivedFrom":subQ1}),1.0]])]});}
            var Q23;
            {var subQ0=sQuery(id+"F4.wireOp",EDGE,"a4a6697a-bb5a-402e-a274-67412d378b00");var subQ1=sQuery(id+"F4.wireOp",EDGE,"E69.left");var subQ2=makeQuery(id+"F4.imprint","INTERSECT",VERTEX,{"derivedFrom":[subQ1,subQ0]});Q23=makeQuery(id+"F4.imprint","IMPRINT",FACE,{"disambiguationData":[TD([[makeQuery(id+"F4.imprint","IMPRINT",EDGE,{"disambiguationData":[TD([[subQ2,-1.0]])],"derivedFrom":subQ1}),1.0]])]});}
            extrude(context, id + "F9", {"entities" : qUnion([Q0, Q1, Q2, Q3, Q4, Q5, Q6, Q7, Q8, Q9, Q10, Q11, Q12, Q13, Q14, Q15, Q16, Q17, Q18, Q19, Q20, Q21, Q22, Q23]), "operationType" : NewBodyOperationType.ADD, "depth" : 12.7 * mm});
        }
    });
